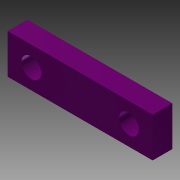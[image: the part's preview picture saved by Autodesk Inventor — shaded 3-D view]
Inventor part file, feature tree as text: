
AUTODESK INVENTOR PART (.ipt)
format: ipt  version: 2013 (Build 170138000, 138)  size: 78,848 bytes
history: native  units: mm
features: other x1, extrude x1, sketch x1
ambient origin geometry x8: Origin, YZ Plane, XZ Plane, XY Plane, X Axis, Y Axis, Z Axis, Center Point
feature tree (3):
  other  "ソリッド1"
  extrude  "押し出し1"  Depth=14.8mm
  sketch  "スケッチ1"
